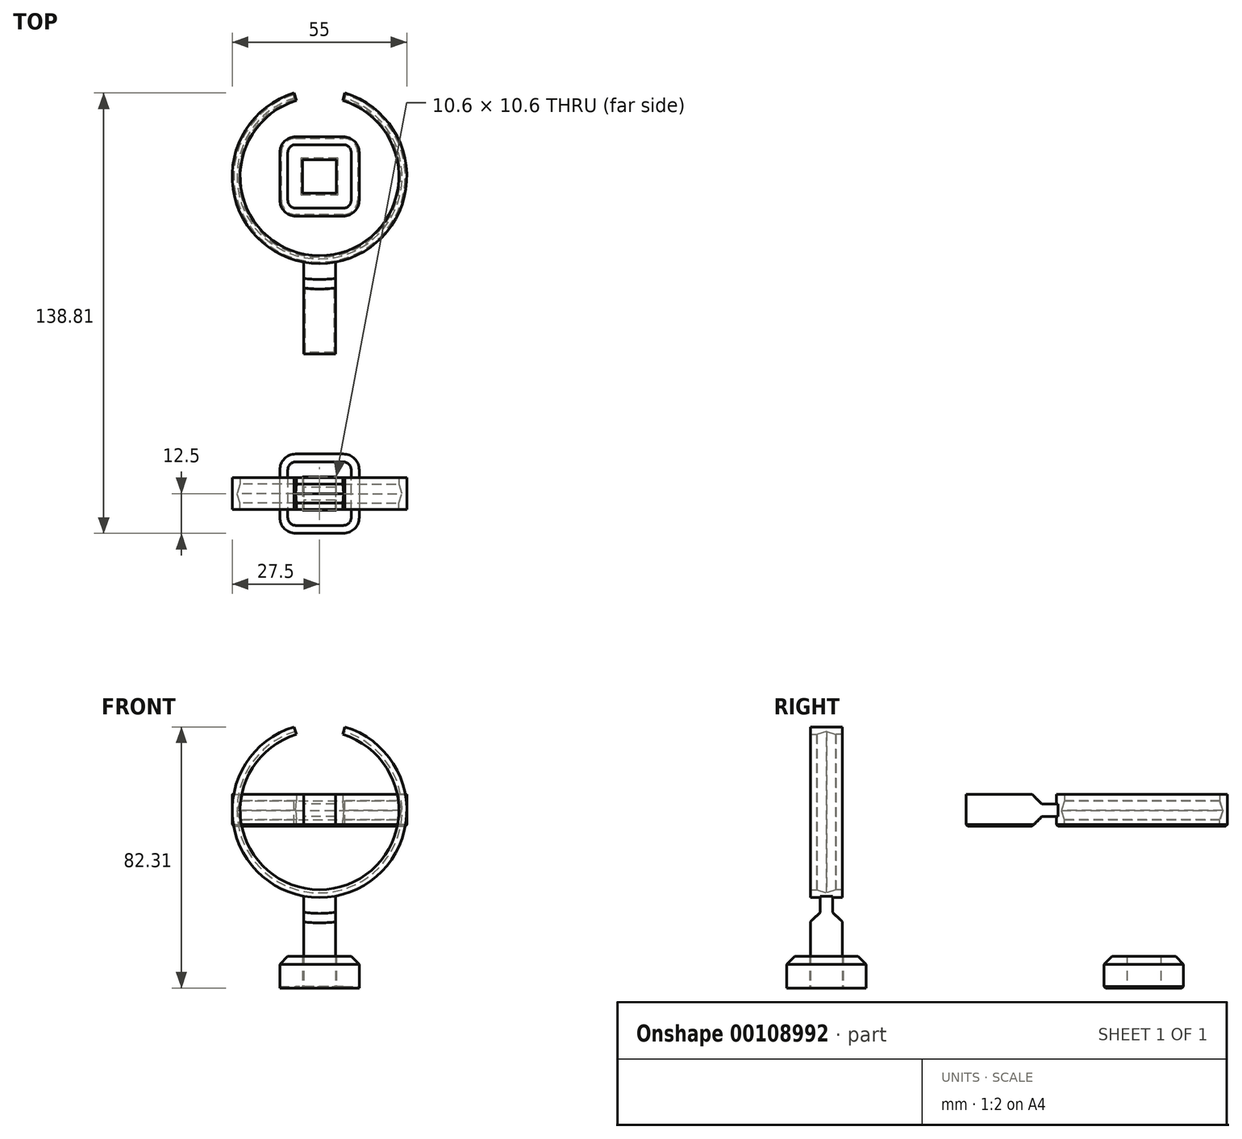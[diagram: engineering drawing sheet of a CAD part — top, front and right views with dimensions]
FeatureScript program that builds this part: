
annotation { "Feature Type Name" : "Feature", "Feature Type Description" : "" }
export const myFeature = defineFeature(function(context is Context, id is Id, definition is map)
    precondition{}
    {
        {
            var Q0;
            Q0=qCreatedBy(makeId("Front.planeOp"),FACE);
            var sketch = newSketch(context, id + "F0", { "sketchPlane" : qUnion([Q0])});
            skArc(sketch, "E0", {"start": v(-7.28, 23.92) * mm, "mid": v(-0.02, -25) * mm, "end": v(7.31, 23.9) * mm});
            skArc(sketch, "E1.0", {"start": v(-8, 26.3) * mm, "mid": v(-0.02, -27.5) * mm, "end": v(8.04, 26.3) * mm});
            skLineSegment(sketch, "E2", {"start": v(-8, 26.3) * mm, "end": v(-7.28, 23.92) * mm});
            skLineSegment(sketch, "E3", {"start": v(8.04, 26.3) * mm, "end": v(7.31, 23.9) * mm});
            skSolve(sketch);
        }
        {
            var Q0;
            Q0=qCreatedBy(makeId("Front.planeOp"),FACE);
            var sketch = newSketch(context, id + "F1", { "sketchPlane" : qUnion([Q0])});
            skLineSegment(sketch, "E4", {"start": v(-14.5, 0) * mm, "end": v(14.18, 0) * mm, "construction": true});
            skSolve(sketch);
        }
        {
            var Q0;
            Q0 = qSketchRegion(id + "F0", true);
            extrude(context, id + "F2", {"entities" : qUnion([Q0]), "oppositeDirection" : true, "depth" : 5 * mm});
        }
        {
            var Q0;
            Q0=makeQuery(id+"F2.opExtrude","CAP_EDGE",EDGE,{"disambiguationData":[OSD([sQuery(id+"F0.wireOp",EDGE,"E0")])],"isStart":true});
            chamfer(context, id + "F3", {"entities" : qUnion([Q0]), "chamferType" : ChamferType.TWO_OFFSETS, "width1" : 1 * mm, "oppositeDirection" : true, "width2" : 3 * mm, "tangentPropagation" : true});
        }
        {
            var Q0;
            Q0=makeQuery(id+"F2.opExtrude","CAP_FACE",FACE,{"disambiguationData":[OSD([sQuery(id+"F0.wireOp",EDGE,"E0"),sQuery(id+"F0.wireOp",EDGE,"E1.0"),sQuery(id+"F0.wireOp",EDGE,"E2"),sQuery(id+"F0.wireOp",EDGE,"E3")])],"isStart":true});
            var sketch = newSketch(context, id + "F4", { "sketchPlane" : qUnion([Q0])});
            skArc(sketch, "E5.0", {"start": v(7.6, 24.86) * mm, "mid": v(-0.02, -26) * mm, "end": v(-7.57, 24.87) * mm});
            skLineSegment(sketch, "E6.bottom", {"start": v(-5, -26) * mm, "end": v(5, -26) * mm});
            skLineSegment(sketch, "E6.top", {"start": v(-5, -56) * mm, "end": v(5, -56) * mm});
            skLineSegment(sketch, "E6.left", {"start": v(-5, -26) * mm, "end": v(-5, -56) * mm});
            skLineSegment(sketch, "E6.right", {"start": v(5, -26) * mm, "end": v(5, -56) * mm});
            skPoint(sketch, "E7", {"position": v(0, -26) * mm});
            skSolve(sketch);
        }
        {
            var Q0;
            Q0 = qSketchRegion(id + "F4", true);
            extrude(context, id + "F5", {"entities" : qUnion([Q0]), "operationType" : NewBodyOperationType.ADD, "oppositeDirection" : true, "depth" : 5 * mm});
        }
        {
            var Q0;
            Q0=makeQuery(id+"F5.boolean.opBoolean","MERGE",FACE,{"derivedFrom":[makeQuery(id+"F2.opExtrude","CAP_FACE",FACE,{"disambiguationData":[OSD([sQuery(id+"F0.wireOp",EDGE,"E0"),sQuery(id+"F0.wireOp",EDGE,"E1.0"),sQuery(id+"F0.wireOp",EDGE,"E2"),sQuery(id+"F0.wireOp",EDGE,"E3")])],"isStart":false}),makeQuery(id+"F5.opExtrude","CAP_FACE",FACE,{"disambiguationData":[OSD([sQuery(id+"F4.wireOp",EDGE,"E6.bottom"),sQuery(id+"F4.wireOp",EDGE,"E6.top"),sQuery(id+"F4.wireOp",EDGE,"E6.left"),sQuery(id+"F4.wireOp",EDGE,"E6.right")])],"isStart":false})]});
            var sketch = newSketch(context, id + "F6", { "sketchPlane" : qUnion([Q0])});
            skArc(sketch, "E8.0", {"start": v(5, -27.04) * mm, "mid": v(0, -27.5) * mm, "end": v(-5, -27.04) * mm});
            skArc(sketch, "E9.0", {"start": v(5, -32.11) * mm, "mid": v(0, -32.5) * mm, "end": v(-5, -32.11) * mm});
            skArc(sketch, "E10.0.0", {"start": v(-8.04, 26.3) * mm, "mid": v(-27.46, -1.57) * mm, "end": v(-5, -27.04) * mm});
            skLineSegment(sketch, "E10.0.1", {"start": v(-5, -27.04) * mm, "end": v(-5, -32.11) * mm});
            skLineSegment(sketch, "E10.0.3", {"start": v(5, -32.11) * mm, "end": v(5, -27.04) * mm});
            skArc(sketch, "E10.0.4", {"start": v(5, -27.04) * mm, "mid": v(27.46, -1.55) * mm, "end": v(8, 26.3) * mm});
            skPoint(sketch, "E10.0.2.end.orphan", {"position": v(5, -56) * mm});
            skPoint(sketch, "E11.orphan", {"position": v(-5, -56) * mm});
            skPoint(sketch, "E12.orphan", {"position": v(-8.04, 26.3) * mm});
            skPoint(sketch, "E13.orphan", {"position": v(8, 26.3) * mm});
            skPoint(sketch, "E10.0.7.start.orphan", {"position": v(-7.31, 23.9) * mm});
            skPoint(sketch, "E10.0.5.end.orphan", {"position": v(7.28, 23.92) * mm});
            skSolve(sketch);
        }
        {
            var Q0;
            Q0 = qSketchRegion(id + "F6", true);
            extrude(context, id + "F7", {"entities" : qUnion([Q0]), "operationType" : NewBodyOperationType.REMOVE, "oppositeDirection" : true, "depth" : 3 * mm});
        }
        {
            var Q0;
            Q0=makeQuery(id+"F7.boolean.opBoolean","COPY",EDGE,{"derivedFrom":makeQuery(id+"F7.opExtrude","CAP_EDGE",EDGE,{"disambiguationData":[OSD([sQuery(id+"F6.wireOp",EDGE,"E9.0")])],"isStart":true})});
            chamfer(context, id + "F8", {"entities" : qUnion([Q0]), "width" : 3 * mm, "tangentPropagation" : true});
        }
        {
            var Q0;
            Q0=makeQuery(id+"F2.opExtrude","SWEPT_BODY",BODY,{"disambiguationData":[OSD([sQuery(id+"F0.wireOp",EDGE,"E0"),sQuery(id+"F0.wireOp",EDGE,"E1.0"),sQuery(id+"F0.wireOp",EDGE,"E2"),sQuery(id+"F0.wireOp",EDGE,"E3")])]});
            var Q1;
            Q1=qCreatedBy(makeId("Front.planeOp"),FACE);
            mirror(context, id + "F9", {"operationType" : NewBodyOperationType.ADD, "entities" : qUnion([Q0]), "mirrorPlane" : qUnion([Q1])});
        }
        {
            var Q0;
            {var subQ0=makeQuery(id+"F5.opExtrude","SWEPT_FACE",FACE,{"disambiguationData":[OSD([sQuery(id+"F4.wireOp",EDGE,"E6.top")])]});Q0=makeQuery(id+"F9.boolean.opBoolean","MERGE",FACE,{"derivedFrom":[subQ0,makeQuery(id+"F9.opPattern","COPY",FACE,{"derivedFrom":subQ0,"instanceName":"1"})]});}
            var sketch = newSketch(context, id + "F10", { "sketchPlane" : qUnion([Q0])});
            skLineSegment(sketch, "E14.0.0", {"start": v(5, -5) * mm, "end": v(5, 5) * mm});
            skLineSegment(sketch, "E14.0.1", {"start": v(5, 5) * mm, "end": v(-5, 5) * mm});
            skLineSegment(sketch, "E14.0.2", {"start": v(-5, 5) * mm, "end": v(-5, -5) * mm});
            skLineSegment(sketch, "E14.0.3", {"start": v(-5, -5) * mm, "end": v(5, -5) * mm});
            skLineSegment(sketch, "E15.0", {"start": v(5.3, -5.3) * mm, "end": v(5.3, 5.3) * mm});
            skLineSegment(sketch, "E15.1", {"start": v(-5.3, -5.3) * mm, "end": v(5.3, -5.3) * mm});
            skLineSegment(sketch, "E15.2", {"start": v(-5.3, 5.3) * mm, "end": v(-5.3, -5.3) * mm});
            skLineSegment(sketch, "E15.3", {"start": v(5.3, 5.3) * mm, "end": v(-5.3, 5.3) * mm});
            skLineSegment(sketch, "E16.0", {"start": v(12.5, -7.5) * mm, "end": v(12.5, 7.5) * mm});
            skLineSegment(sketch, "E16.1", {"start": v(-7.5, -12.5) * mm, "end": v(7.5, -12.5) * mm});
            skLineSegment(sketch, "E16.2", {"start": v(-12.5, 7.5) * mm, "end": v(-12.5, -7.5) * mm});
            skLineSegment(sketch, "E16.3", {"start": v(7.5, 12.5) * mm, "end": v(-7.5, 12.5) * mm});
            skPoint(sketch, "E17.visualSharp", {"position": v(12.5, -12.5) * mm});
            skArc(sketch, "E17.filletArc", {"start": v(7.5, -12.5) * mm, "mid": v(11.04, -11.04) * mm, "end": v(12.5, -7.5) * mm});
            skPoint(sketch, "E18.visualSharp", {"position": v(-12.5, -12.5) * mm});
            skArc(sketch, "E18.filletArc", {"start": v(-12.5, -7.5) * mm, "mid": v(-11.04, -11.04) * mm, "end": v(-7.5, -12.5) * mm});
            skPoint(sketch, "E19.visualSharp", {"position": v(-12.5, 12.5) * mm});
            skArc(sketch, "E19.filletArc", {"start": v(-7.5, 12.5) * mm, "mid": v(-11.04, 11.04) * mm, "end": v(-12.5, 7.5) * mm});
            skPoint(sketch, "E20.visualSharp", {"position": v(12.5, 12.5) * mm});
            skArc(sketch, "E20.filletArc", {"start": v(12.5, 7.5) * mm, "mid": v(11.04, 11.04) * mm, "end": v(7.5, 12.5) * mm});
            skSolve(sketch);
        }
        {
            var Q0;
            Q0 = qSketchRegion(id + "F10", true);
            extrude(context, id + "F11", {"entities" : qUnion([Q0]), "oppositeDirection" : true, "depth" : 10 * mm});
        }
        {
            var Q0;
            Q0=makeQuery(id+"F11.opExtrude","CAP_EDGE",EDGE,{"disambiguationData":[OSD([sQuery(id+"F10.wireOp",EDGE,"E16.3")])],"isStart":false});
            chamfer(context, id + "F12", {"entities" : qUnion([Q0]), "width" : 2.5 * mm, "tangentPropagation" : true});
        }
        {
            var Q0;
            Q0=makeQuery(id+"F2.opExtrude","SWEPT_BODY",BODY,{"disambiguationData":[OSD([sQuery(id+"F0.wireOp",EDGE,"E0"),sQuery(id+"F0.wireOp",EDGE,"E1.0"),sQuery(id+"F0.wireOp",EDGE,"E2"),sQuery(id+"F0.wireOp",EDGE,"E3")])]});
            var Q1;
            Q1=makeQuery(id+"F11.opExtrude","SWEPT_BODY",BODY,{"disambiguationData":[OSD([sQuery(id+"F10.wireOp",EDGE,"E15.0"),sQuery(id+"F10.wireOp",EDGE,"E15.1"),sQuery(id+"F10.wireOp",EDGE,"E15.2"),sQuery(id+"F10.wireOp",EDGE,"E15.3"),sQuery(id+"F10.wireOp",EDGE,"E16.0"),sQuery(id+"F10.wireOp",EDGE,"E16.1"),sQuery(id+"F10.wireOp",EDGE,"E16.2"),sQuery(id+"F10.wireOp",EDGE,"E16.3"),sQuery(id+"F10.wireOp",EDGE,"E17.filletArc"),sQuery(id+"F10.wireOp",EDGE,"E18.filletArc"),sQuery(id+"F10.wireOp",EDGE,"E19.filletArc"),sQuery(id+"F10.wireOp",EDGE,"E20.filletArc")])]});
            transform(context, id + "F13", {"entities" : qUnion([Q0, Q1]), "transformType" : TransformType.TRANSLATION_3D, "dx" : 0 * mm, "dy" : -100 * mm, "dz" : 0 * mm, "makeCopy" : true});
        }
        {
            var Q0;
            Q0=makeQuery(id+"F2.opExtrude","SWEPT_BODY",BODY,{"disambiguationData":[OSD([sQuery(id+"F0.wireOp",EDGE,"E0"),sQuery(id+"F0.wireOp",EDGE,"E1.0"),sQuery(id+"F0.wireOp",EDGE,"E2"),sQuery(id+"F0.wireOp",EDGE,"E3")])]});
            var Q1;
            Q1=sQuery(id+"F1.wireOp",EDGE,"E4");
            transform(context, id + "F14", {"entities" : qUnion([Q0]), "transformType" : TransformType.ROTATION, "transformAxis" : qUnion([Q1]), "angle" : 90 * degree, "oppositeDirection" : true, "makeCopy" : false});
        }
        {
            var Q0;
            {var subQ0=sQuery(id+"F4.wireOp",EDGE,"E6.top");var subQ1=sQuery(id+"F4.wireOp",EDGE,"E6.left");var subQ2=sQuery(id+"F4.wireOp",EDGE,"E6.right");Q0=makeQuery(id+"F7.boolean.opBoolean","SPLIT",FACE,{"disambiguationData":[TD([makeQuery(id+"F5.opExtrude","SWEPT_FACE",FACE,{"disambiguationData":[OSD([subQ0])]})])],"derivedFrom":makeQuery(id+"F5.boolean.opBoolean","MERGE",FACE,{"derivedFrom":[makeQuery(id+"F2.opExtrude","CAP_FACE",FACE,{"disambiguationData":[OSD([sQuery(id+"F0.wireOp",EDGE,"E0"),sQuery(id+"F0.wireOp",EDGE,"E1.0"),sQuery(id+"F0.wireOp",EDGE,"E2"),sQuery(id+"F0.wireOp",EDGE,"E3")])],"isStart":false}),makeQuery(id+"F5.opExtrude","CAP_FACE",FACE,{"disambiguationData":[OSD([sQuery(id+"F4.wireOp",EDGE,"E6.bottom"),subQ0,subQ1,subQ2])],"isStart":false})]})});}
            var Q1;
            {var subQ0=sQuery(id+"F0.wireOp",EDGE,"E3");var subQ1=sQuery(id+"F0.wireOp",EDGE,"E2");var subQ2=sQuery(id+"F0.wireOp",EDGE,"E1.0");var subQ3=sQuery(id+"F0.wireOp",EDGE,"E0");Q1=makeQuery(id+"F7.boolean.opBoolean","SPLIT",FACE,{"disambiguationData":[TD([makeQuery(id+"F2.opExtrude","SWEPT_FACE",FACE,{"disambiguationData":[OSD([subQ3])]})])],"derivedFrom":makeQuery(id+"F5.boolean.opBoolean","MERGE",FACE,{"derivedFrom":[makeQuery(id+"F2.opExtrude","CAP_FACE",FACE,{"disambiguationData":[OSD([subQ3,subQ2,subQ1,subQ0])],"isStart":false}),makeQuery(id+"F5.opExtrude","CAP_FACE",FACE,{"disambiguationData":[OSD([sQuery(id+"F4.wireOp",EDGE,"E6.bottom"),sQuery(id+"F4.wireOp",EDGE,"E6.top"),sQuery(id+"F4.wireOp",EDGE,"E6.left"),sQuery(id+"F4.wireOp",EDGE,"E6.right")])],"isStart":false})]})});}
            var Q2;
            Q2=makeQuery(id+"F11.opExtrude","CAP_FACE",FACE,{"disambiguationData":[OSD([sQuery(id+"F10.wireOp",EDGE,"E15.0"),sQuery(id+"F10.wireOp",EDGE,"E15.1"),sQuery(id+"F10.wireOp",EDGE,"E15.2"),sQuery(id+"F10.wireOp",EDGE,"E15.3"),sQuery(id+"F10.wireOp",EDGE,"E16.0"),sQuery(id+"F10.wireOp",EDGE,"E16.1"),sQuery(id+"F10.wireOp",EDGE,"E16.2"),sQuery(id+"F10.wireOp",EDGE,"E16.3"),sQuery(id+"F10.wireOp",EDGE,"E17.filletArc"),sQuery(id+"F10.wireOp",EDGE,"E18.filletArc"),sQuery(id+"F10.wireOp",EDGE,"E19.filletArc"),sQuery(id+"F10.wireOp",EDGE,"E20.filletArc")])],"isStart":true});
            chamfer(context, id + "F15", {"entities" : qUnion([Q0, Q1, Q2]), "width" : 0.5 * mm, "tangentPropagation" : true});
        }
    });
